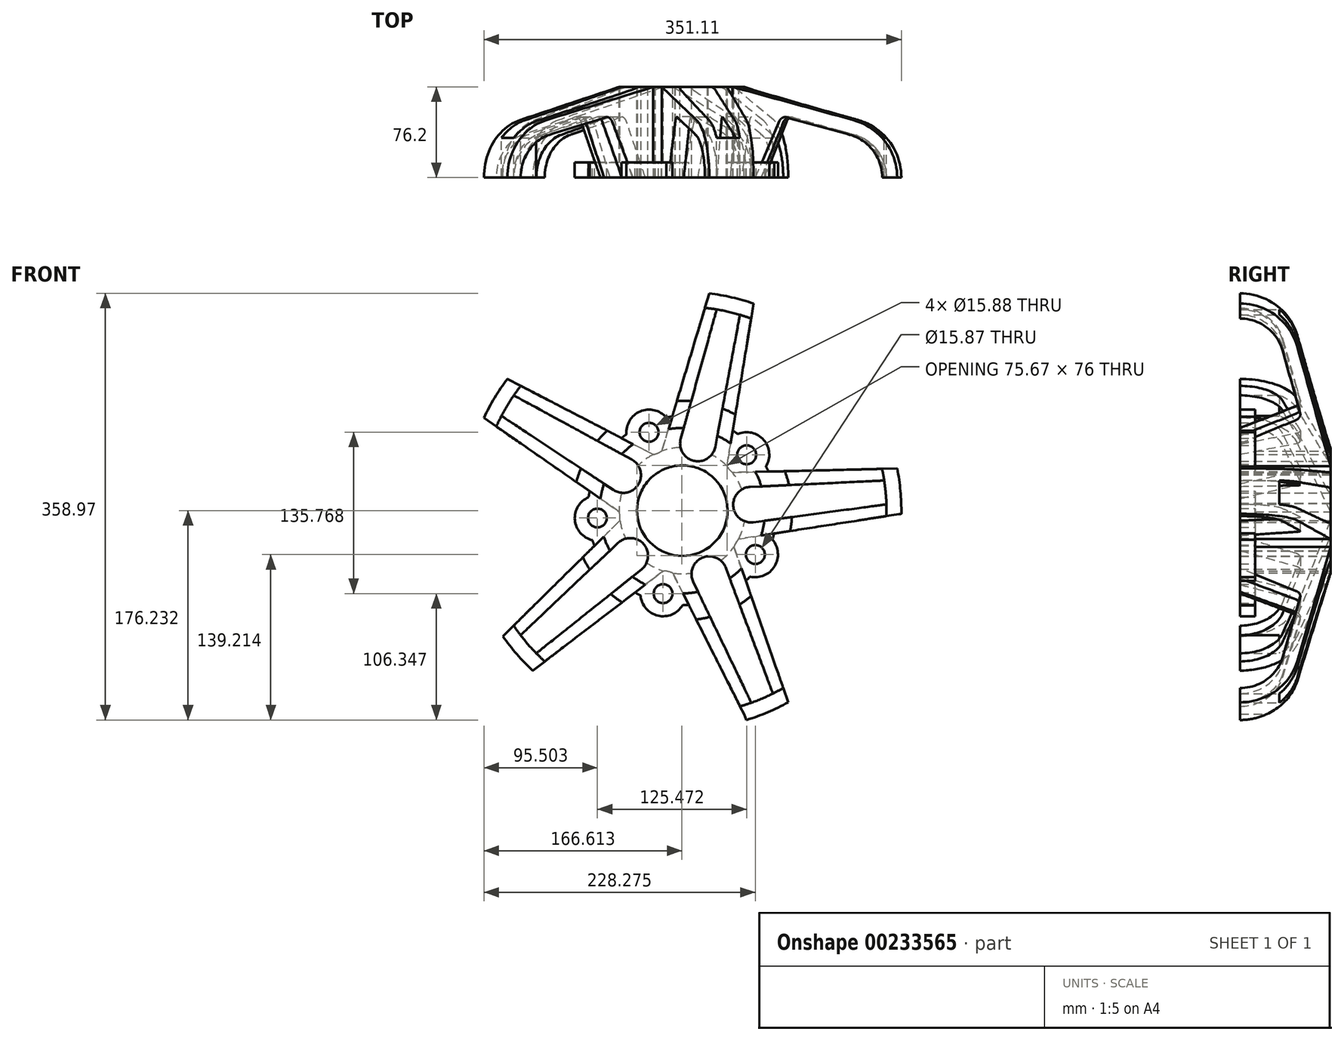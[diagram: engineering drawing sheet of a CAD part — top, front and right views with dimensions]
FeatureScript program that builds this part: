
annotation { "Feature Type Name" : "Feature", "Feature Type Description" : "" }
export const myFeature = defineFeature(function(context is Context, id is Id, definition is map)
    precondition{}
    {
        {
            var Q0;
            Q0=qCreatedBy(makeId("Front.planeOp"),FACE);
            var sketch = newSketch(context, id + "F0", { "sketchPlane" : qUnion([Q0])});
            skCircle(sketch, "E0", {"center": v(0, 0) * mm, "radius": 317.5 * mm});
            skCircle(sketch, "E1", {"center": v(0, 0) * mm, "radius": 203.2 * mm});
            skCircle(sketch, "E2", {"center": v(0, 0) * mm, "radius": 197.17 * mm});
            skCircle(sketch, "E3.0", {"center": v(0, 0) * mm, "radius": 184.47 * mm});
            skCircle(sketch, "E4", {"center": v(0, 0) * mm, "radius": 38.1 * mm});
            skCircle(sketch, "E5", {"center": v(-27.96, 65.96) * mm, "radius": 7.94 * mm});
            skCircle(sketch, "E6", {"center": v(54.1, 46.98) * mm, "radius": 7.94 * mm});
            skCircle(sketch, "E7", {"center": v(-71.38, -6.21) * mm, "radius": 7.94 * mm});
            skCircle(sketch, "E8", {"center": v(-16.15, -69.8) * mm, "radius": 7.94 * mm});
            skCircle(sketch, "E9", {"center": v(61.4, -36.94) * mm, "radius": 7.94 * mm});
            skLineSegment(sketch, "E10", {"start": v(61.4, -36.94) * mm, "end": v(61.39, -36.93) * mm, "construction": true});
            skLineSegment(sketch, "E11", {"start": v(61.4, -36.94) * mm, "end": v(61.4, -36.93) * mm, "construction": true});
            skLineSegment(sketch, "E12", {"start": v(7.15, 30.9) * mm, "end": v(7.23, 31.26) * mm, "construction": true});
            skLineSegment(sketch, "E13", {"start": v(7.23, 31.26) * mm, "end": v(7.15, 30.9) * mm});
            skLineSegment(sketch, "E14", {"start": v(7.8, -18.39) * mm, "end": v(7.82, -18.44) * mm});
            skLineSegment(sketch, "E15", {"start": v(-24.04, -20.88) * mm, "end": v(-24.12, -20.95) * mm});
            skArc(sketch, "E16", {"start": v(-116.03, -127.12) * mm, "mid": v(-38.6, -167.72) * mm, "end": v(48.77, -165.06) * mm});
            skLineSegment(sketch, "E17", {"start": v(60.14, 175.43) * mm, "end": v(37.53, 37.56) * mm});
            skLineSegment(sketch, "E18.trimOffspring", {"start": v(-23.25, 30.18) * mm, "end": v(-23.15, 30.52) * mm});
            skLineSegment(sketch, "E19.0", {"start": v(-126.04, -134.7) * mm, "end": v(-126.79, -135.34) * mm});
            skLineSegment(sketch, "E19.1", {"start": v(7.89, -18.38) * mm, "end": v(7.82, -18.44) * mm});
            skLineSegment(sketch, "E20", {"start": v(-147.37, 110.95) * mm, "end": v(-24.42, 47.25) * mm});
            skLineSegment(sketch, "E21", {"start": v(-167.08, 78.2) * mm, "end": v(-53.1, -0.86) * mm});
            skLineSegment(sketch, "E22", {"start": v(-5.94, 37.67) * mm, "end": v(-5.99, 37.63) * mm});
            skLineSegment(sketch, "E23", {"start": v(-126.79, -135.34) * mm, "end": v(-16.03, -50.75) * mm});
            skPoint(sketch, "E24.orphan", {"position": v(-49.67, 29.88) * mm});
            skLineSegment(sketch, "E25.0", {"start": v(-7.3, -31.58) * mm, "end": v(-6.68, -33.05) * mm});
            skLineSegment(sketch, "E26.0", {"start": v(51.86, -171.16) * mm, "end": v(54.06, -176.37) * mm});
            skLineSegment(sketch, "E27.0", {"start": v(27.67, -16.48) * mm, "end": v(27.96, -17.16) * mm});
            skLineSegment(sketch, "E28.1", {"start": v(7.8, -18.39) * mm, "end": v(7.89, -18.38) * mm});
            skLineSegment(sketch, "E29", {"start": v(-37.73, 6.23) * mm, "end": v(-37.62, 6.02) * mm});
            skLineSegment(sketch, "E30", {"start": v(21.75, 31.6) * mm, "end": v(21.9, 31.17) * mm});
            skLineSegment(sketch, "E31", {"start": v(181.03, 35.46) * mm, "end": v(42.2, 32.1) * mm});
            skLineSegment(sketch, "E32", {"start": v(184.45, -2.61) * mm, "end": v(47.55, -23.84) * mm});
            skPoint(sketch, "E33.orphan", {"position": v(-43.76, -38) * mm});
            skLineSegment(sketch, "E34.trimOffspring", {"start": v(-24.12, -20.95) * mm, "end": v(-23.94, -21.08) * mm});
            skLineSegment(sketch, "E35.trimOffspring", {"start": v(-24.04, -20.88) * mm, "end": v(-23.94, -21.08) * mm});
            skLineSegment(sketch, "E36.trimOffspring", {"start": v(-37.56, 6.4) * mm, "end": v(-37.73, 6.23) * mm});
            skLineSegment(sketch, "E37.trimOffspring", {"start": v(-22.8, 30.53) * mm, "end": v(-23.15, 30.52) * mm});
            skLineSegment(sketch, "E38.trimOffspring", {"start": v(-17.49, -33.85) * mm, "end": v(-17.45, -33.93) * mm});
            skLineSegment(sketch, "E39.trimOffspring", {"start": v(-7.97, -32.15) * mm, "end": v(-6.68, -33.05) * mm});
            skLineSegment(sketch, "E40.trimOffspring", {"start": v(-17.37, -33.91) * mm, "end": v(-17.45, -33.93) * mm});
            skLineSegment(sketch, "E41.trimOffspring", {"start": v(-7.3, -31.58) * mm, "end": v(-8.4, -32.52) * mm});
            skLineSegment(sketch, "E42.trimOffspring", {"start": v(-7, -32.3) * mm, "end": v(-8.4, -32.52) * mm});
            skLineSegment(sketch, "E43.trimOffspring", {"start": v(11.99, -29.36) * mm, "end": v(12.33, -29.1) * mm});
            skLineSegment(sketch, "E44.trimOffspring", {"start": v(-52.45, -8.33) * mm, "end": v(-151.06, -105.87) * mm});
            skLineSegment(sketch, "E45.trimOffspring", {"start": v(-17.2, 50.24) * mm, "end": v(22.81, 183.05) * mm});
            skLineSegment(sketch, "E46.trimOffspring", {"start": v(-5.94, 37.67) * mm, "end": v(-5.89, 37.64) * mm});
            skArc(sketch, "E47.trimOffspring", {"start": v(-156.77, 71.04) * mm, "mid": v(-171.46, -14.92) * mm, "end": v(-142.14, -97.05) * mm});
            skLineSegment(sketch, "E48.trimOffspring", {"start": v(0.55, -38.1) * mm, "end": v(0.57, -38.08) * mm});
            skLineSegment(sketch, "E49.trimOffspring", {"start": v(-8.03, -52.57) * mm, "end": v(51.86, -171.16) * mm});
            skLineSegment(sketch, "E50.trimOffspring", {"start": v(12.42, -29.3) * mm, "end": v(11.99, -29.36) * mm});
            skPoint(sketch, "E51.orphan", {"position": v(22.62, -53.37) * mm});
            skArc(sketch, "E52.trimOffspring", {"start": v(85.06, -149.62) * mm, "mid": v(147.61, -88.5) * mm, "end": v(172.05, -4.53) * mm});
            skLineSegment(sketch, "E53.trimOffspring", {"start": v(43.46, -30.52) * mm, "end": v(89.2, -161.47) * mm});
            skLineSegment(sketch, "E54.trimOffspring", {"start": v(36.5, -10.63) * mm, "end": v(36.55, -10.76) * mm});
            skLineSegment(sketch, "E55.trimOffspring", {"start": v(27.67, -16.48) * mm, "end": v(29.03, -16.35) * mm});
            skLineSegment(sketch, "E56.trimOffspring", {"start": v(12.33, -29.1) * mm, "end": v(12.42, -29.3) * mm});
            skLineSegment(sketch, "E57.trimOffspring", {"start": v(27.96, -17.16) * mm, "end": v(29.03, -16.35) * mm});
            skLineSegment(sketch, "E58.trimOffspring", {"start": v(36.5, -10.63) * mm, "end": v(36.6, -10.56) * mm});
            skArc(sketch, "E59.trimOffspring", {"start": v(168.48, 35.16) * mm, "mid": v(129.78, 113.04) * mm, "end": v(57.95, 162.06) * mm});
            skLineSegment(sketch, "E60.trimOffspring", {"start": v(21.75, 31.6) * mm, "end": v(21.3, 31.6) * mm});
            skLineSegment(sketch, "E61.trimOffspring", {"start": v(25.26, 21.57) * mm, "end": v(25.29, 21.5) * mm});
            skLineSegment(sketch, "E62.trimOffspring", {"start": v(7.23, 31.26) * mm, "end": v(6.48, 31.24) * mm});
            skLineSegment(sketch, "E63.trimOffspring", {"start": v(25.16, 21.56) * mm, "end": v(25.29, 21.5) * mm});
            skLineSegment(sketch, "E64.trimOffspring", {"start": v(25.16, 21.56) * mm, "end": v(25.26, 21.57) * mm});
            skLineSegment(sketch, "E65.trimOffspring", {"start": v(6.48, 31.24) * mm, "end": v(7.15, 30.9) * mm});
            skPoint(sketch, "E66.orphan", {"position": v(13.07, 56.47) * mm});
            skArc(sketch, "E67.trimOffspring", {"start": v(19.2, 171.04) * mm, "mid": v(-67.15, 158.47) * mm, "end": v(-136.23, 105.18) * mm});
            skLineSegment(sketch, "E68.2", {"start": v(61.4, -36.93) * mm, "end": v(61.39, -36.93) * mm});
            skArc(sketch, "E69", {"start": v(-1.31, 60.46) * mm, "mid": v(9.7, 41.93) * mm, "end": v(27.73, 53.73) * mm});
            skArc(sketch, "E70", {"start": v(57.03, 19.93) * mm, "mid": v(42.88, 3.67) * mm, "end": v(59.74, -9.76) * mm});
            skArc(sketch, "E71", {"start": v(37, -49.4) * mm, "mid": v(17.39, -39.4) * mm, "end": v(9.17, -59.82) * mm});
            skArc(sketch, "E72", {"start": v(-34.47, -49.68) * mm, "mid": v(-32.5, -28.22) * mm, "end": v(-54.02, -27.17) * mm});
            skArc(sketch, "E73", {"start": v(-57.9, 17.43) * mm, "mid": v(-36.88, 22.19) * mm, "end": v(-42.53, 42.98) * mm});
            skLineSegment(sketch, "E74", {"start": v(-136.07, -104.83) * mm, "end": v(-54.02, -27.17) * mm});
            skLineSegment(sketch, "E75", {"start": v(-122.86, -120.04) * mm, "end": v(-34.47, -49.68) * mm});
            skLineSegment(sketch, "E76", {"start": v(-141.74, 97.02) * mm, "end": v(-42.53, 42.98) * mm});
            skLineSegment(sketch, "E77", {"start": v(-152.13, 79.75) * mm, "end": v(-57.9, 17.43) * mm});
            skLineSegment(sketch, "E78", {"start": v(48.47, 164.79) * mm, "end": v(27.73, 53.73) * mm});
            skLineSegment(sketch, "E79", {"start": v(28.91, 169.32) * mm, "end": v(-1.31, 60.46) * mm});
            skLineSegment(sketch, "E80", {"start": v(169.88, 25.37) * mm, "end": v(57.03, 19.93) * mm});
            skLineSegment(sketch, "E81", {"start": v(171.68, 5.3) * mm, "end": v(59.74, -9.76) * mm});
            skLineSegment(sketch, "E82", {"start": v(58.02, -161.67) * mm, "end": v(9.17, -59.82) * mm});
            skLineSegment(sketch, "E83", {"start": v(36.08, -46.92) * mm, "end": v(76.19, -153.95) * mm});
            skCircle(sketch, "E84", {"center": v(534.68, -34.22) * mm, "radius": 12.7 * mm});
            skArc(sketch, "E85.0", {"start": v(48.47, 164.79) * mm, "mid": v(38.76, 167.34) * mm, "end": v(28.91, 169.32) * mm});
            skArc(sketch, "E86.trimOffspring", {"start": v(171.68, 5.3) * mm, "mid": v(171.08, 15.36) * mm, "end": v(169.88, 25.37) * mm});
            skArc(sketch, "E87.trimOffspring", {"start": v(58.02, -161.67) * mm, "mid": v(67.22, -158.07) * mm, "end": v(76.19, -153.95) * mm});
            skArc(sketch, "E88.trimOffspring", {"start": v(-136.07, -104.83) * mm, "mid": v(-129.69, -112.63) * mm, "end": v(-122.86, -120.04) * mm});
            skArc(sketch, "E89.trimOffspring", {"start": v(-141.74, 97.02) * mm, "mid": v(-147.2, 88.54) * mm, "end": v(-152.13, 79.75) * mm});
            skArc(sketch, "E90", {"start": v(-78.77, 11.35) * mm, "mid": v(-90.36, -7.86) * mm, "end": v(-75.63, -24.78) * mm});
            skArc(sketch, "E91", {"start": v(-35.13, -71.41) * mm, "mid": v(-20.44, -88.36) * mm, "end": v(0.2, -79.58) * mm});
            skArc(sketch, "E92", {"start": v(57.06, -55.48) * mm, "mid": v(77.72, -46.75) * mm, "end": v(75.75, -24.4) * mm});
            skArc(sketch, "E93", {"start": v(37.53, 37.56) * mm, "mid": v(39.6, 34.61) * mm, "end": v(42.2, 32.1) * mm});
            skArc(sketch, "E94", {"start": v(-13.55, 78.42) * mm, "mid": v(-35.4, 83.5) * mm, "end": v(-46.94, 64.27) * mm});
            skArc(sketch, "E95", {"start": v(46.62, 64.5) * mm, "mid": v(44.54, 65.95) * mm, "end": v(42.42, 67.34) * mm});
            skArc(sketch, "E96.trimOffspring", {"start": v(-24.42, 47.25) * mm, "mid": v(-20.66, 48.37) * mm, "end": v(-17.2, 50.24) * mm});
            skArc(sketch, "E97.trimOffspring", {"start": v(70.4, 37.12) * mm, "mid": v(68.48, 59.47) * mm, "end": v(46.62, 64.5) * mm});
            skArc(sketch, "E98.trimOffspring", {"start": v(31.36, 73.15) * mm, "mid": v(17.95, 77.53) * mm, "end": v(3.97, 79.49) * mm});
            skArc(sketch, "E99.trimOffspring", {"start": v(-8.5, 79.13) * mm, "mid": v(-11.03, 78.82) * mm, "end": v(-13.55, 78.42) * mm});
            skArc(sketch, "E100.trimOffspring", {"start": v(-46.94, 64.27) * mm, "mid": v(-49.02, 62.7) * mm, "end": v(-51.06, 61.05) * mm});
            skArc(sketch, "E101.trimOffspring", {"start": v(-52.45, -8.33) * mm, "mid": v(-52.4, -4.56) * mm, "end": v(-53.1, -0.86) * mm});
            skArc(sketch, "E102.trimOffspring", {"start": v(-75.63, -24.78) * mm, "mid": v(-74.8, -27.18) * mm, "end": v(-73.9, -29.55) * mm});
            skArc(sketch, "E103.trimOffspring", {"start": v(-8.03, -52.57) * mm, "mid": v(-11.93, -51.23) * mm, "end": v(-16.03, -50.75) * mm});
            skArc(sketch, "E104.trimOffspring", {"start": v(0.2, -79.58) * mm, "mid": v(2.86, -79.53) * mm, "end": v(5.51, -79.4) * mm});
            skArc(sketch, "E105.trimOffspring", {"start": v(-68.36, -40.74) * mm, "mid": v(-60.09, -52.18) * mm, "end": v(-49.92, -61.98) * mm});
            skArc(sketch, "E106.trimOffspring", {"start": v(-39.8, -68.91) * mm, "mid": v(-37.5, -70.2) * mm, "end": v(-35.13, -71.41) * mm});
            skArc(sketch, "E107.trimOffspring", {"start": v(17.7, -77.6) * mm, "mid": v(31.07, -73.27) * mm, "end": v(43.48, -66.66) * mm});
            skArc(sketch, "E108.trimOffspring", {"start": v(53.4, -59) * mm, "mid": v(55.26, -57.27) * mm, "end": v(57.06, -55.48) * mm});
            skArc(sketch, "E109.trimOffspring", {"start": v(47.55, -23.84) * mm, "mid": v(45.16, -26.97) * mm, "end": v(43.46, -30.52) * mm});
            skArc(sketch, "E110.trimOffspring", {"start": v(75.75, -24.4) * mm, "mid": v(76.53, -21.84) * mm, "end": v(77.22, -19.24) * mm});
            skArc(sketch, "E111.trimOffspring", {"start": v(68.1, -41.2) * mm, "mid": v(68.2, -41.03) * mm, "end": v(68.3, -40.85) * mm});
            skArc(sketch, "E112.trimOffspring", {"start": v(-59.88, 52.43) * mm, "mid": v(-68.2, 41.02) * mm, "end": v(-74.37, 28.32) * mm});
            skArc(sketch, "E113.trimOffspring", {"start": v(-77.89, 16.34) * mm, "mid": v(-78.37, 13.85) * mm, "end": v(-78.77, 11.35) * mm});
            skArc(sketch, "E114.trimOffspring", {"start": v(72.5, 32.84) * mm, "mid": v(71.48, 35) * mm, "end": v(70.4, 37.12) * mm});
            skArc(sketch, "E115.trimOffspring", {"start": v(79.26, -7.14) * mm, "mid": v(79.28, 6.98) * mm, "end": v(76.8, 20.88) * mm});
            skSolve(sketch);
        }
        {
            var Q0;
            {var subQ57=sQuery(id+"F0.wireOp",EDGE,"E18.trimOffspring");Q0=makeQuery(id+"F0.imprint","IMPRINT",FACE,{"disambiguationData":[TD([[makeQuery(id+"F0.imprint","IMPRINT",EDGE,{"derivedFrom":subQ57}),1.0]])]});}
            extrude(context, id + "F1", {"entities" : qUnion([Q0]), "depth" : 76.2 * mm});
        }
        {
            var Q0;
            Q0=makeQuery(id+"F1.opExtrude","SWEPT_FACE",FACE,{"disambiguationData":[OSD([sQuery(id+"F0.wireOp",EDGE,"E53.trimOffspring")])]});
            var sketch = newSketch(context, id + "F2", { "sketchPlane" : qUnion([Q0])});
            skLineSegment(sketch, "E116", {"start": v(-27.93, -144.8) * mm, "end": v(0, -43.15) * mm});
            skArc(sketch, "E117", {"start": v(-31.35, -109.31) * mm, "mid": v(-126.03, -136.35) * mm, "end": v(-27.93, -144.8) * mm});
            skCircle(sketch, "E118.0", {"center": v(-76.2, -131.55) * mm, "radius": 37.36 * mm});
            skLineSegment(sketch, "E119.0", {"start": v(-50.35, -178.49) * mm, "end": v(-49, -173.58) * mm});
            skLineSegment(sketch, "E120.trimOffspring", {"start": v(-40.17, -141.44) * mm, "end": v(-12.25, -39.78) * mm});
            skPoint(sketch, "E121.orphan", {"position": v(-38.1, -181.85) * mm});
            skArc(sketch, "E122", {"start": v(-26.7, -92.43) * mm, "mid": v(-25.27, -86.82) * mm, "end": v(-28.98, -82.38) * mm});
            skLineSegment(sketch, "E123", {"start": v(-28.98, -82.38) * mm, "end": v(-76.2, -62.3) * mm});
            skSolve(sketch);
        }
        {
            var Q0;
            {var subQ1=sQuery(id+"F2.wireOp",EDGE,"E116");Q0=makeQuery(id+"F2.imprint","IMPRINT",FACE,{"disambiguationData":[TD([[makeQuery(id+"F2.imprint","IMPRINT",EDGE,{"derivedFrom":subQ1}),-1.0]])]});}
            var Q1;
            {var subQ0=sQuery(id+"F2.wireOp",EDGE,"E120.trimOffspring");var subQ1=sQuery(id+"F2.wireOp",EDGE,"E117");var subQ2=makeQuery(id+"F2.imprint","INTERSECT",VERTEX,{"derivedFrom":[subQ1,subQ0]});Q1=makeQuery(id+"F2.imprint","IMPRINT",FACE,{"disambiguationData":[TD([[makeQuery(id+"F2.imprint","IMPRINT",EDGE,{"disambiguationData":[TD([[subQ2,-1.0]])],"derivedFrom":subQ1}),-1.0]])]});}
            var Q2;
            {var subQ0=sQuery(id+"F2.wireOp",EDGE,"E120.trimOffspring");var subQ1=sQuery(id+"F2.wireOp",EDGE,"E117");var subQ2=makeQuery(id+"F2.imprint","INTERSECT",VERTEX,{"derivedFrom":[subQ1,subQ0]});Q2=makeQuery(id+"F2.imprint","IMPRINT",FACE,{"disambiguationData":[TD([[makeQuery(id+"F2.imprint","IMPRINT",EDGE,{"disambiguationData":[TD([[subQ2,-1.0]])],"derivedFrom":subQ1}),1.0]])]});}
            var Q3;
            {var subQ0=sQuery(id+"F2.wireOp",EDGE,"E118.0");var subQ1=makeQuery(id+"F2.imprint","INTERSECT",VERTEX,{"derivedFrom":[subQ0,sQuery(id+"F2.wireOp",EDGE,"E120.trimOffspring")]});Q3=makeQuery(id+"F2.imprint","IMPRINT",FACE,{"disambiguationData":[TD([[makeQuery(id+"F2.imprint","IMPRINT",EDGE,{"disambiguationData":[TD([[subQ1,1.0]])],"derivedFrom":subQ0}),1.0]])]});}
            var Q4;
            {var subQ0=sQuery(id+"F0.wireOp",EDGE,"E4");Q4=makeQuery(id+"F1.opExtrude","SWEPT_FACE",FACE,{"disambiguationData":[OSD([subQ0]),TDD([makeQuery(id+"F0.imprint","IMPRINT",EDGE,{"disambiguationData":[TD([[makeQuery(id+"F0.imprint","INTERSECT",VERTEX,{"derivedFrom":[subQ0,sQuery(id+"F0.wireOp",EDGE,"E29")]}),-1.0]])],"derivedFrom":subQ0})])]});}
            revolve(context, id + "F3", {"operationType" : NewBodyOperationType.REMOVE, "entities" : qUnion([Q0, Q1, Q2, Q3]), "axis" : qUnion([Q4]), "revolveType" : RevolveType.FULL, "oppositeDirection" : true});
        }
        {
            var Q0;
            Q0=makeQuery(id+"F0.imprint","IMPRINT",FACE,{"disambiguationData":[TD([[makeQuery(id+"F0.imprint","IMPRINT",EDGE,{"derivedFrom":sQuery(id+"F0.wireOp",EDGE,"E7")}),-1.0]])]});
            var Q1;
            Q1=makeQuery(id+"F0.imprint","IMPRINT",FACE,{"disambiguationData":[TD([[makeQuery(id+"F0.imprint","IMPRINT",EDGE,{"derivedFrom":sQuery(id+"F0.wireOp",EDGE,"E8")}),-1.0]])]});
            var Q2;
            Q2=makeQuery(id+"F0.imprint","IMPRINT",FACE,{"disambiguationData":[TD([[makeQuery(id+"F0.imprint","IMPRINT",EDGE,{"derivedFrom":sQuery(id+"F0.wireOp",EDGE,"E92")}),1.0]])]});
            var Q3;
            Q3=makeQuery(id+"F0.imprint","IMPRINT",FACE,{"disambiguationData":[TD([[makeQuery(id+"F0.imprint","IMPRINT",EDGE,{"derivedFrom":sQuery(id+"F0.wireOp",EDGE,"E6")}),-1.0]])]});
            var Q4;
            Q4=makeQuery(id+"F0.imprint","IMPRINT",FACE,{"disambiguationData":[TD([[makeQuery(id+"F0.imprint","IMPRINT",EDGE,{"derivedFrom":sQuery(id+"F0.wireOp",EDGE,"E5")}),-1.0]])]});
            extrude(context, id + "F4", {"entities" : qUnion([Q0, Q1, Q2, Q3, Q4]), "operationType" : NewBodyOperationType.ADD, "depth" : 76.2 * mm, "hasSecondDirection" : true, "secondDirectionOppositeDirection" : false, "secondDirectionDepth" : 63.5 * mm});
        }
    });
